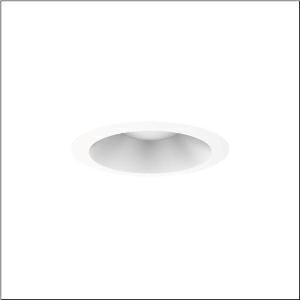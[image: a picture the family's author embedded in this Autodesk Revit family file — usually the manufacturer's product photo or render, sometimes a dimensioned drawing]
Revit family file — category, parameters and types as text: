
# Revit family: lunis_31_midi_51dn157g42
name_source: partatom
category: Lighting Fixtures
units: mm (PartAtom-declared; Revit-internal decimal feet)

## family parameters
Cut with Voids When Loaded = No
Host = Face
Light Source = No
Part Type = Normal
Room Calculation Point = No
Round Connector Dimension = Use Diameter
Shared = No

## types (1)
- Lunis 31 midi (1 x LED, 2150 lm, 17 W, 4000K)
    Apparent Load = 17 VA
    CIE Flux Codes = 89 99 100 100 100
    Color Rendering = 80
    Color Temperature = 4000K
    Default Elevation = 1800 mm
    Description = Lunis 31,  midi, downlight, light control with lens, light emission: direct distribution, LED rated luminous flux: 2.150lm, light colour: 840, mains connection: 220..240V, AC, 50/60Hz, housing, white, protection rating (complete): IP20, protection rating (on room side): IP54, insulation class (complete): insulation class II (safety insulation), certification: CE, packaging unit: 1 piece
    Height = 0 mm  [stored 0 ft]
    Lamp = 1 x LED
    Lamp Light Flux = 2150 lm
    Lamp Power = 17 W
    Lamp count = 1
    Length = 259 mm
    Luminous efficacy = 126 lm/W
    Manufacturer = Siteco
    ModVariant = No
    Model = 51DN157G42
    Mounting Place = Ceiling
    Mounting Type = Recessed
    Number of Poles = 1
    OnlyDefault = Yes
    Power Factor = 1
    Product Name = Lunis 31 midi
    Product group = downlight
    ProductGroupID = 400
    Protection Class = Protection class II
    Protection Degree = IP 20
    RLX_Detail_Level = 1
    RLX_Emergency_Light_Flux = 0 lm
    RLX_Emergency_Type = 0
    RLX_Emergency_Type_DB = No
    RlxData = <blob elided: 23721 chars, md5=7b2b7b56>
    Socket = socket
    Standby Power = 0 W
    System Light Flux = 2150 lm
    System Power = 17 W
    Type Comments = Product without accessories
    Type Image = l_1006711.jpg
    URL = http://relux.com
    VarID = ---
    Voltage = 0 V
    Weight = 0.00 kg
    Width = 0 mm  [stored 0 ft]

note: [stored X ft] marks values corroborated as IEEE doubles in the binary element streams (Revit-internal decimal feet)

## geometry (parser evidence)
native form markers: Blend x4, Sweep x10
no freeform markers — native parametric forms only
